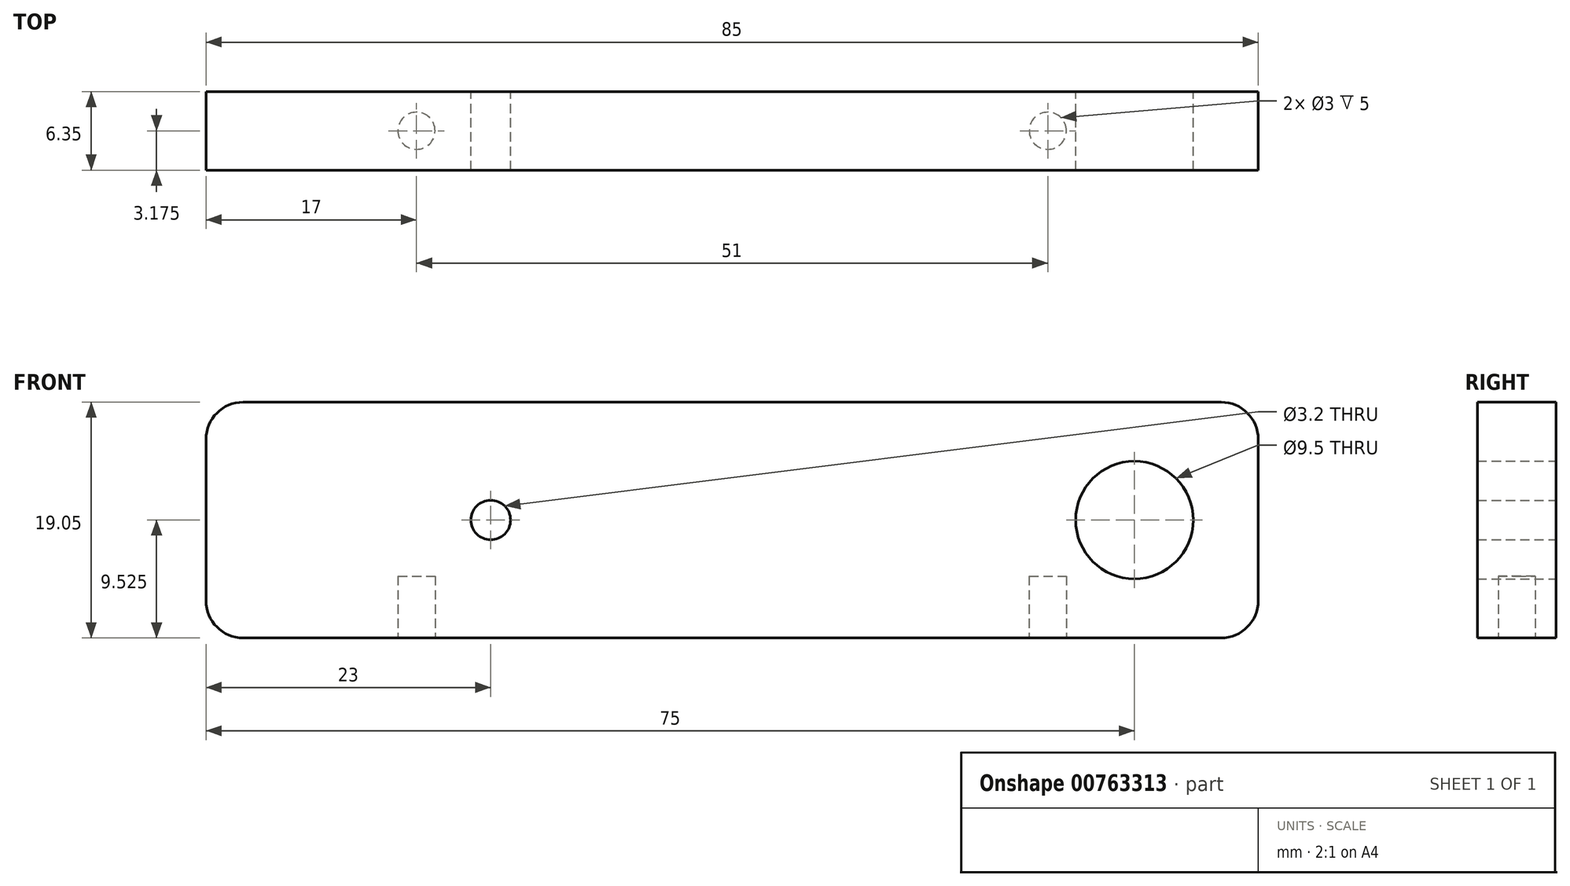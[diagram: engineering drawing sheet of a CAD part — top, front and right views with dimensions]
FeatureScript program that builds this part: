
annotation { "Feature Type Name" : "Feature", "Feature Type Description" : "" }
export const myFeature = defineFeature(function(context is Context, id is Id, definition is map)
    precondition{}
    {
        {
            var Q0;
            Q0=qCreatedBy(makeId("Front.planeOp"),FACE);
            var sketch = newSketch(context, id + "F0", { "sketchPlane" : qUnion([Q0])});
            skLineSegment(sketch, "E0.bottom", {"start": v(0, 0) * mm, "end": v(85, 0) * mm});
            skLineSegment(sketch, "E0.top", {"start": v(0, 19.05) * mm, "end": v(85, 19.05) * mm});
            skLineSegment(sketch, "E0.left", {"start": v(0, 0) * mm, "end": v(0, 19.05) * mm});
            skLineSegment(sketch, "E0.right", {"start": v(85, 0) * mm, "end": v(85, 19.05) * mm});
            skCircle(sketch, "E1", {"center": v(23, 9.52) * mm, "radius": 1.6 * mm});
            skPoint(sketch, "E1.centerSnap0", {"position": v(85, 9.53) * mm});
            skCircle(sketch, "E2", {"center": v(75, 9.52) * mm, "radius": 4.75 * mm});
            skSolve(sketch);
        }
        {
            var Q0;
            Q0=makeQuery(id+"F0.imprint","IMPRINT",FACE,{"disambiguationData":[TD([[makeQuery(id+"F0.imprint","IMPRINT",EDGE,{"derivedFrom":sQuery(id+"F0.wireOp",EDGE,"E0.bottom")}),1.0]])]});
            extrude(context, id + "F1", {"entities" : qUnion([Q0]), "depth" : 6.35 * mm, "offsetDistance" : 25 * mm});
        }
        {
            var Q0;
            Q0=makeQuery(id+"F1.opExtrude","SWEPT_EDGE",EDGE,{"disambiguationData":[OSD([sQuery(id+"F0.wireOp",EDGE,"E0.top"),sQuery(id+"F0.wireOp",EDGE,"E0.right")])]});
            var Q1;
            Q1=makeQuery(id+"F1.opExtrude","SWEPT_EDGE",EDGE,{"disambiguationData":[OSD([sQuery(id+"F0.wireOp",EDGE,"E0.bottom"),sQuery(id+"F0.wireOp",EDGE,"E0.right")])]});
            var Q2;
            Q2=makeQuery(id+"F1.opExtrude","SWEPT_EDGE",EDGE,{"disambiguationData":[OSD([sQuery(id+"F0.wireOp",EDGE,"E0.top"),sQuery(id+"F0.wireOp",EDGE,"E0.left")])]});
            var Q3;
            Q3=makeQuery(id+"F1.opExtrude","SWEPT_EDGE",EDGE,{"disambiguationData":[OSD([sQuery(id+"F0.wireOp",EDGE,"E0.bottom"),sQuery(id+"F0.wireOp",EDGE,"E0.left")])]});
            fillet(context, id + "F2", {"entities" : qUnion([Q0, Q1, Q2, Q3]), "radius" : 3 * mm, "tangentPropagation" : true, "allowEdgeOverflow" : false});
        }
        {
            var Q0;
            Q0=makeQuery(id+"F1.opExtrude","SWEPT_FACE",FACE,{"disambiguationData":[OSD([sQuery(id+"F0.wireOp",EDGE,"E0.bottom")])]});
            var sketch = newSketch(context, id + "F3", { "sketchPlane" : qUnion([Q0])});
            skCircle(sketch, "E3", {"center": v(68, 3.17) * mm, "radius": 1.5 * mm});
            skPoint(sketch, "E3.centerSnap0", {"position": v(82, 3.17) * mm});
            skCircle(sketch, "E4", {"center": v(17, 3.17) * mm, "radius": 1.5 * mm});
            skSolve(sketch);
        }
        {
            var Q0;
            Q0=makeQuery(id+"F3.imprint","IMPRINT",FACE,{"disambiguationData":[TD([[makeQuery(id+"F3.imprint","IMPRINT",EDGE,{"derivedFrom":sQuery(id+"F3.wireOp",EDGE,"E4")}),1.0]])]});
            var Q1;
            Q1=makeQuery(id+"F3.imprint","IMPRINT",FACE,{"disambiguationData":[TD([[makeQuery(id+"F3.imprint","IMPRINT",EDGE,{"derivedFrom":sQuery(id+"F3.wireOp",EDGE,"E3")}),1.0]])]});
            extrude(context, id + "F4", {"entities" : qUnion([Q0, Q1]), "operationType" : NewBodyOperationType.REMOVE, "oppositeDirection" : true, "depth" : 5 * mm, "offsetDistance" : 25 * mm});
        }
    });
